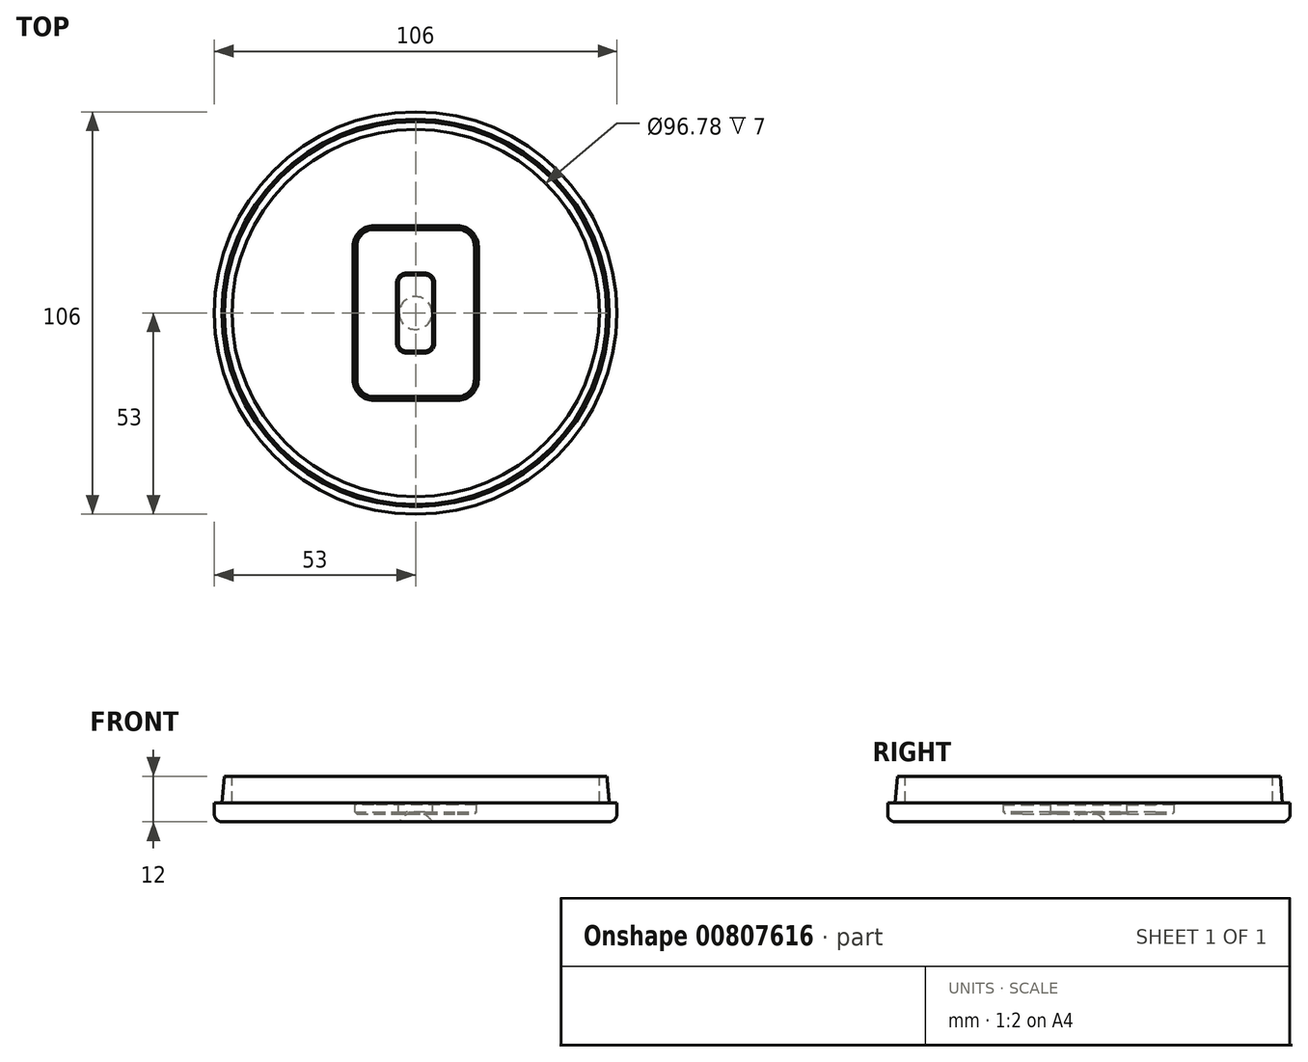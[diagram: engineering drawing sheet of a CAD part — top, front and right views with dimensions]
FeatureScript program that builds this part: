
annotation { "Feature Type Name" : "Feature", "Feature Type Description" : "" }
export const myFeature = defineFeature(function(context is Context, id is Id, definition is map)
    precondition{}
    {
        {
            var Q0;
            Q0=qCreatedBy(makeId("Front.planeOp"),FACE);
            var sketch = newSketch(context, id + "F0", { "sketchPlane" : qUnion([Q0])});
            skLineSegment(sketch, "E0", {"start": v(0, 0) * mm, "end": v(0, 2.5) * mm, "construction": true});
            skLineSegment(sketch, "E1", {"start": v(0, 0) * mm, "end": v(0, -2.5) * mm, "construction": true});
            skCircle(sketch, "E2", {"center": v(0, -2.5) * mm, "radius": 5 * mm});
            skLineSegment(sketch, "E3", {"start": v(4.33, 0) * mm, "end": v(53, 0) * mm});
            skLineSegment(sketch, "E4", {"start": v(53, 0) * mm, "end": v(53, 5) * mm});
            skLineSegment(sketch, "E5", {"start": v(53, 5) * mm, "end": v(51, 5) * mm});
            skLineSegment(sketch, "E6", {"start": v(51, 5) * mm, "end": v(50.39, 12) * mm});
            skLineSegment(sketch, "E7", {"start": v(50.39, 12) * mm, "end": v(48.39, 12) * mm});
            skLineSegment(sketch, "E8", {"start": v(48.39, 12) * mm, "end": v(48.39, 5) * mm});
            skLineSegment(sketch, "E9", {"start": v(48.39, 5) * mm, "end": v(0, 5) * mm});
            skLineSegment(sketch, "E10", {"start": v(0, 5) * mm, "end": v(0, 2.5) * mm});
            skSolve(sketch);
        }
        {
            var Q0;
            {var subQ0=sQuery(id+"F0.wireOp",EDGE,"E3");Q0=makeQuery(id+"F0.imprint","IMPRINT",FACE,{"disambiguationData":[TD([[makeQuery(id+"F0.imprint","IMPRINT",EDGE,{"derivedFrom":subQ0}),1.0]])]});}
            var Q1;
            Q1=sQuery(id+"F0.wireOp",EDGE,"E10");
            revolve(context, id + "F1", {"surfaceOperationType" : NewSurfaceOperationType.NEW, "entities" : qUnion([Q0]), "axis" : qUnion([Q1]), "revolveType" : RevolveType.FULL});
        }
        {
            var Q0;
            Q0=makeQuery(id+"F1.opRevolve","SWEPT_EDGE",EDGE,{"disambiguationData":[OSD([sQuery(id+"F0.wireOp",EDGE,"E3"),sQuery(id+"F0.wireOp",EDGE,"E4")])]});
            fillet(context, id + "F2", {"entities" : qUnion([Q0]), "radius" : 2 * mm, "tangentPropagation" : true, "allowEdgeOverflow" : false});
        }
        {
            var Q0;
            Q0=makeQuery(id+"F1.opRevolve","SWEPT_FACE",FACE,{"disambiguationData":[OSD([sQuery(id+"F0.wireOp",EDGE,"E9")])]});
            var sketch = newSketch(context, id + "F3", { "sketchPlane" : qUnion([Q0])});
            skLineSegment(sketch, "E11.bottom", {"start": v(4.5, 10) * mm, "end": v(-4.5, 10) * mm});
            skLineSegment(sketch, "E11.top", {"start": v(4.5, -10) * mm, "end": v(-4.5, -10) * mm});
            skLineSegment(sketch, "E11.left", {"start": v(4.5, 10) * mm, "end": v(4.5, -10) * mm});
            skLineSegment(sketch, "E11.right", {"start": v(-4.5, 10) * mm, "end": v(-4.5, -10) * mm});
            skPoint(sketch, "E11.middle", {"position": v(0, 0) * mm});
            skLineSegment(sketch, "E12.bottom", {"start": v(16, 22.5) * mm, "end": v(-16, 22.5) * mm});
            skLineSegment(sketch, "E12.top", {"start": v(16, -22.5) * mm, "end": v(-16, -22.5) * mm});
            skLineSegment(sketch, "E12.left", {"start": v(16, 22.5) * mm, "end": v(16, -22.5) * mm});
            skLineSegment(sketch, "E12.right", {"start": v(-16, 22.5) * mm, "end": v(-16, -22.5) * mm});
            skSolve(sketch);
        }
        {
            var Q0;
            Q0 = qSketchRegion(id + "F3", true);
            extrude(context, id + "F4", {"entities" : qUnion([Q0]), "operationType" : NewBodyOperationType.REMOVE, "oppositeDirection" : true, "depth" : 3 * mm, "offsetDistance" : 25 * mm});
        }
        {
            var Q0;
            Q0=makeQuery(id+"F4.boolean.opBoolean","COPY",EDGE,{"derivedFrom":makeQuery(id+"F4.opExtrude","SWEPT_EDGE",EDGE,{"disambiguationData":[OSD([sQuery(id+"F3.wireOp",EDGE,"E12.bottom"),sQuery(id+"F3.wireOp",EDGE,"E12.right")])]})});
            var Q1;
            Q1=makeQuery(id+"F4.boolean.opBoolean","COPY",EDGE,{"derivedFrom":makeQuery(id+"F4.opExtrude","SWEPT_EDGE",EDGE,{"disambiguationData":[OSD([sQuery(id+"F3.wireOp",EDGE,"E12.bottom"),sQuery(id+"F3.wireOp",EDGE,"E12.left")])]})});
            var Q2;
            Q2=makeQuery(id+"F4.boolean.opBoolean","COPY",EDGE,{"derivedFrom":makeQuery(id+"F4.opExtrude","SWEPT_EDGE",EDGE,{"disambiguationData":[OSD([sQuery(id+"F3.wireOp",EDGE,"E12.top"),sQuery(id+"F3.wireOp",EDGE,"E12.left")])]})});
            var Q3;
            Q3=makeQuery(id+"F4.boolean.opBoolean","COPY",EDGE,{"derivedFrom":makeQuery(id+"F4.opExtrude","SWEPT_EDGE",EDGE,{"disambiguationData":[OSD([sQuery(id+"F3.wireOp",EDGE,"E12.top"),sQuery(id+"F3.wireOp",EDGE,"E12.right")])]})});
            fillet(context, id + "F5", {"entities" : qUnion([Q0, Q1, Q2, Q3]), "radius" : 5 * mm, "tangentPropagation" : true, "allowEdgeOverflow" : false});
        }
        {
            var Q0;
            Q0=makeQuery(id+"F4.boolean.opBoolean","COPY",EDGE,{"derivedFrom":makeQuery(id+"F4.opExtrude","SWEPT_EDGE",EDGE,{"disambiguationData":[OSD([sQuery(id+"F3.wireOp",EDGE,"E11.bottom"),sQuery(id+"F3.wireOp",EDGE,"E11.right")])]})});
            var Q1;
            Q1=makeQuery(id+"F4.boolean.opBoolean","COPY",EDGE,{"derivedFrom":makeQuery(id+"F4.opExtrude","SWEPT_EDGE",EDGE,{"disambiguationData":[OSD([sQuery(id+"F3.wireOp",EDGE,"E11.bottom"),sQuery(id+"F3.wireOp",EDGE,"E11.left")])]})});
            var Q2;
            Q2=makeQuery(id+"F4.boolean.opBoolean","COPY",EDGE,{"derivedFrom":makeQuery(id+"F4.opExtrude","SWEPT_EDGE",EDGE,{"disambiguationData":[OSD([sQuery(id+"F3.wireOp",EDGE,"E11.top"),sQuery(id+"F3.wireOp",EDGE,"E11.left")])]})});
            var Q3;
            Q3=makeQuery(id+"F4.boolean.opBoolean","COPY",EDGE,{"derivedFrom":makeQuery(id+"F4.opExtrude","SWEPT_EDGE",EDGE,{"disambiguationData":[OSD([sQuery(id+"F3.wireOp",EDGE,"E11.top"),sQuery(id+"F3.wireOp",EDGE,"E11.right")])]})});
            fillet(context, id + "F6", {"entities" : qUnion([Q0, Q1, Q2, Q3]), "radius" : 2 * mm, "tangentPropagation" : true, "allowEdgeOverflow" : false});
        }
        {
            var Q0;
            Q0=makeQuery(id+"F4.boolean.opBoolean","COPY",EDGE,{"derivedFrom":makeQuery(id+"F4.opExtrude","CAP_EDGE",EDGE,{"disambiguationData":[OSD([sQuery(id+"F3.wireOp",EDGE,"E11.left")])],"isStart":false})});
            var Q1;
            Q1=makeQuery(id+"F4.boolean.opBoolean","COPY",EDGE,{"derivedFrom":makeQuery(id+"F4.opExtrude","CAP_EDGE",EDGE,{"disambiguationData":[OSD([sQuery(id+"F3.wireOp",EDGE,"E12.bottom")])],"isStart":false})});
            var Q2;
            Q2=makeQuery(id+"F4.boolean.opBoolean","COPY",EDGE,{"derivedFrom":makeQuery(id+"F4.opExtrude","CAP_EDGE",EDGE,{"disambiguationData":[OSD([sQuery(id+"F3.wireOp",EDGE,"E12.bottom")])],"isStart":true})});
            chamfer(context, id + "F7", {"entities" : qUnion([Q0, Q1, Q2]), "width" : 0.5 * mm, "tangentPropagation" : true});
        }
    });
